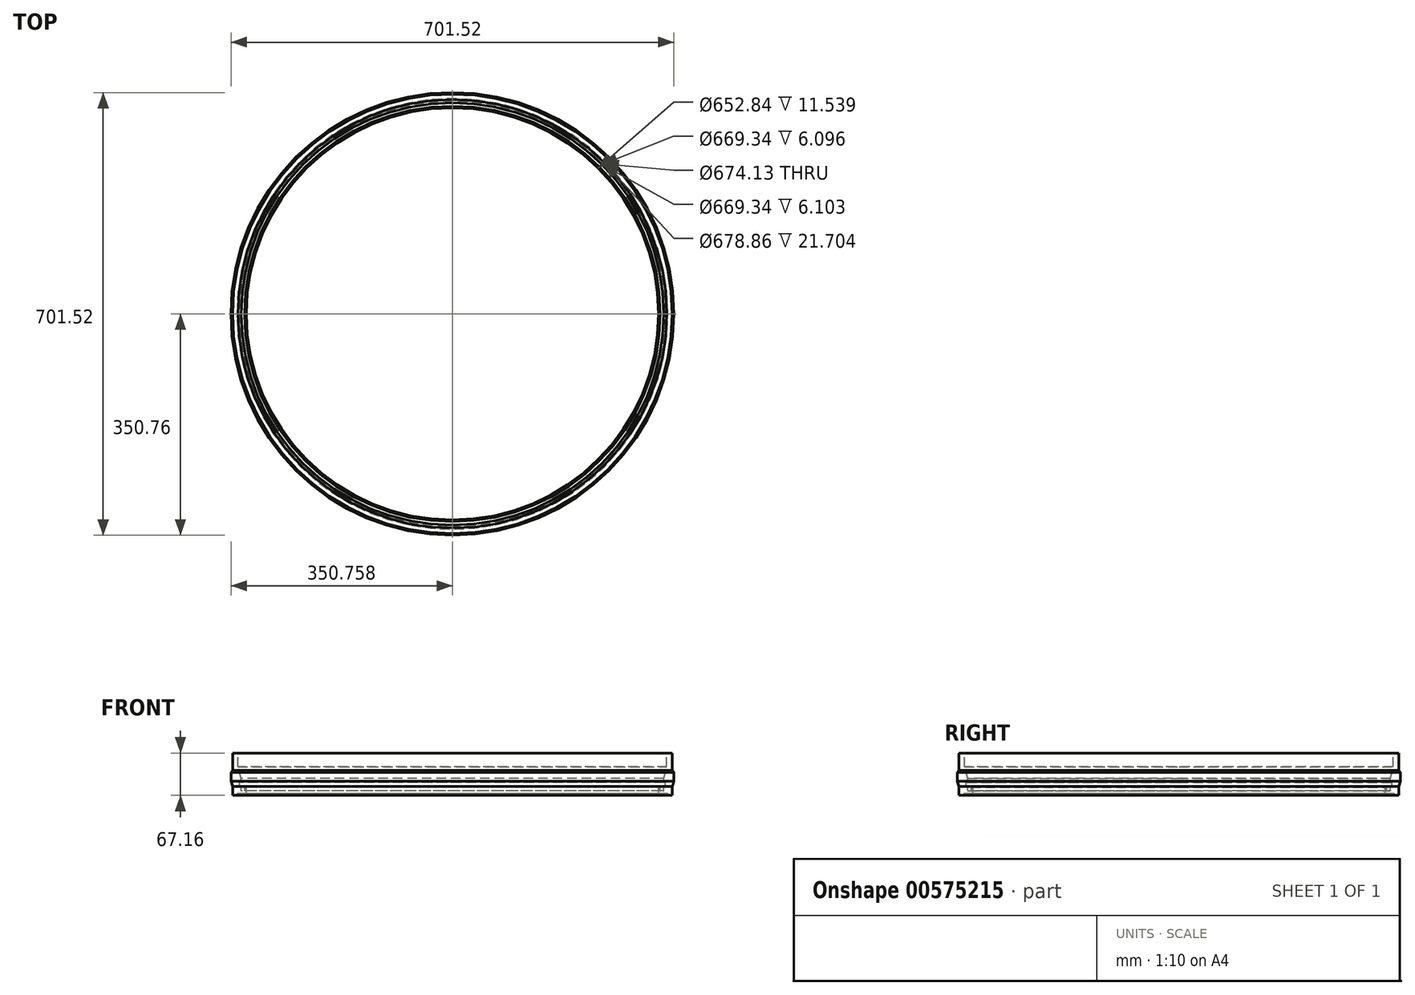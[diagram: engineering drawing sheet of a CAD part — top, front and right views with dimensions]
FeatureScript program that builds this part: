
annotation { "Feature Type Name" : "Feature", "Feature Type Description" : "" }
export const myFeature = defineFeature(function(context is Context, id is Id, definition is map)
    precondition{}
    {
        {
            var Q0;
            Q0=qCreatedBy(makeId("Front.planeOp"),FACE);
            var sketch = newSketch(context, id + "F0", { "sketchPlane" : qUnion([Q0])});
            skLineSegment(sketch, "E0", {"start": v(0, 0) * mm, "end": v(0, -27.56) * mm});
            skLineSegment(sketch, "E1", {"start": v(0, -27.56) * mm, "end": v(-2.54, -30.5) * mm});
            skLineSegment(sketch, "E2", {"start": v(-2.54, -30.5) * mm, "end": v(-2.54, -44.68) * mm});
            skLineSegment(sketch, "E3", {"start": v(-2.54, -44.68) * mm, "end": v(0, -52.98) * mm});
            skLineSegment(sketch, "E4", {"start": v(0, -52.98) * mm, "end": v(0, -67.16) * mm});
            skLineSegment(sketch, "E5", {"start": v(0, -67.16) * mm, "end": v(7.1, -67.16) * mm});
            skLineSegment(sketch, "E6", {"start": v(0, 0) * mm, "end": v(8.79, 0) * mm});
            skLineSegment(sketch, "E7", {"start": v(8.79, 0) * mm, "end": v(8.79, -21.7) * mm});
            skLineSegment(sketch, "E8", {"start": v(8.79, -21.7) * mm, "end": v(13.55, -40.38) * mm});
            skLineSegment(sketch, "E9", {"start": v(13.55, -40.38) * mm, "end": v(13.55, -46.49) * mm});
            skLineSegment(sketch, "E10", {"start": v(13.55, -46.49) * mm, "end": v(11.58, -46.49) * mm});
            skLineSegment(sketch, "E11", {"start": v(11.16, -46.9) * mm, "end": v(11.16, -52.77) * mm});
            skLineSegment(sketch, "E12", {"start": v(11.58, -53.2) * mm, "end": v(13.55, -53.2) * mm});
            skLineSegment(sketch, "E13", {"start": v(13.55, -53.2) * mm, "end": v(13.55, -59.29) * mm});
            skLineSegment(sketch, "E14", {"start": v(14.18, -59.92) * mm, "end": v(18.5, -59.92) * mm});
            skLineSegment(sketch, "E15", {"start": v(19.14, -59.29) * mm, "end": v(19.14, -53.93) * mm});
            skLineSegment(sketch, "E16", {"start": v(19.64, -52.54) * mm, "end": v(21.8, -52.54) * mm});
            skLineSegment(sketch, "E17", {"start": v(21.8, -52.54) * mm, "end": v(21.8, -64.07) * mm});
            skLineSegment(sketch, "E18", {"start": v(21.8, -64.07) * mm, "end": v(7.27, -64.07) * mm});
            skLineSegment(sketch, "E19", {"start": v(7.27, -64.07) * mm, "end": v(7.1, -67.16) * mm});
            skLineSegment(sketch, "E20", {"start": v(19.14, -53.93) * mm, "end": v(19.64, -52.54) * mm});
            skPoint(sketch, "E21.visualSharp", {"position": v(13.55, -59.92) * mm});
            skArc(sketch, "E21.filletArc", {"start": v(13.55, -59.29) * mm, "mid": v(13.73, -59.74) * mm, "end": v(14.18, -59.92) * mm});
            skPoint(sketch, "E22.visualSharp", {"position": v(19.14, -59.92) * mm});
            skArc(sketch, "E22.filletArc", {"start": v(18.5, -59.92) * mm, "mid": v(18.95, -59.74) * mm, "end": v(19.14, -59.29) * mm});
            skLineSegment(sketch, "E23", {"start": v(348.22, -34.6) * mm, "end": v(348.22, -79.93) * mm, "construction": true});
            skPoint(sketch, "E24.visualSharp", {"position": v(11.16, -46.49) * mm});
            skArc(sketch, "E24.filletArc", {"start": v(11.58, -46.49) * mm, "mid": v(11.28, -46.6) * mm, "end": v(11.16, -46.9) * mm});
            skPoint(sketch, "E25.visualSharp", {"position": v(11.16, -53.2) * mm});
            skArc(sketch, "E25.filletArc", {"start": v(11.16, -52.77) * mm, "mid": v(11.28, -53.07) * mm, "end": v(11.58, -53.2) * mm});
            skSolve(sketch);
        }
        {
            var Q0;
            Q0=makeQuery(id+"F0.imprint","IMPRINT",FACE,{"disambiguationData":[TD([[makeQuery(id+"F0.imprint","IMPRINT",EDGE,{"derivedFrom":sQuery(id+"F0.wireOp",EDGE,"E0")}),1.0]])]});
            var Q1;
            Q1=sQuery(id+"F0.wireOp",EDGE,"E23");
            revolve(context, id + "F1", {"entities" : qUnion([Q0]), "axis" : qUnion([Q1]), "revolveType" : RevolveType.FULL});
        }
    });
